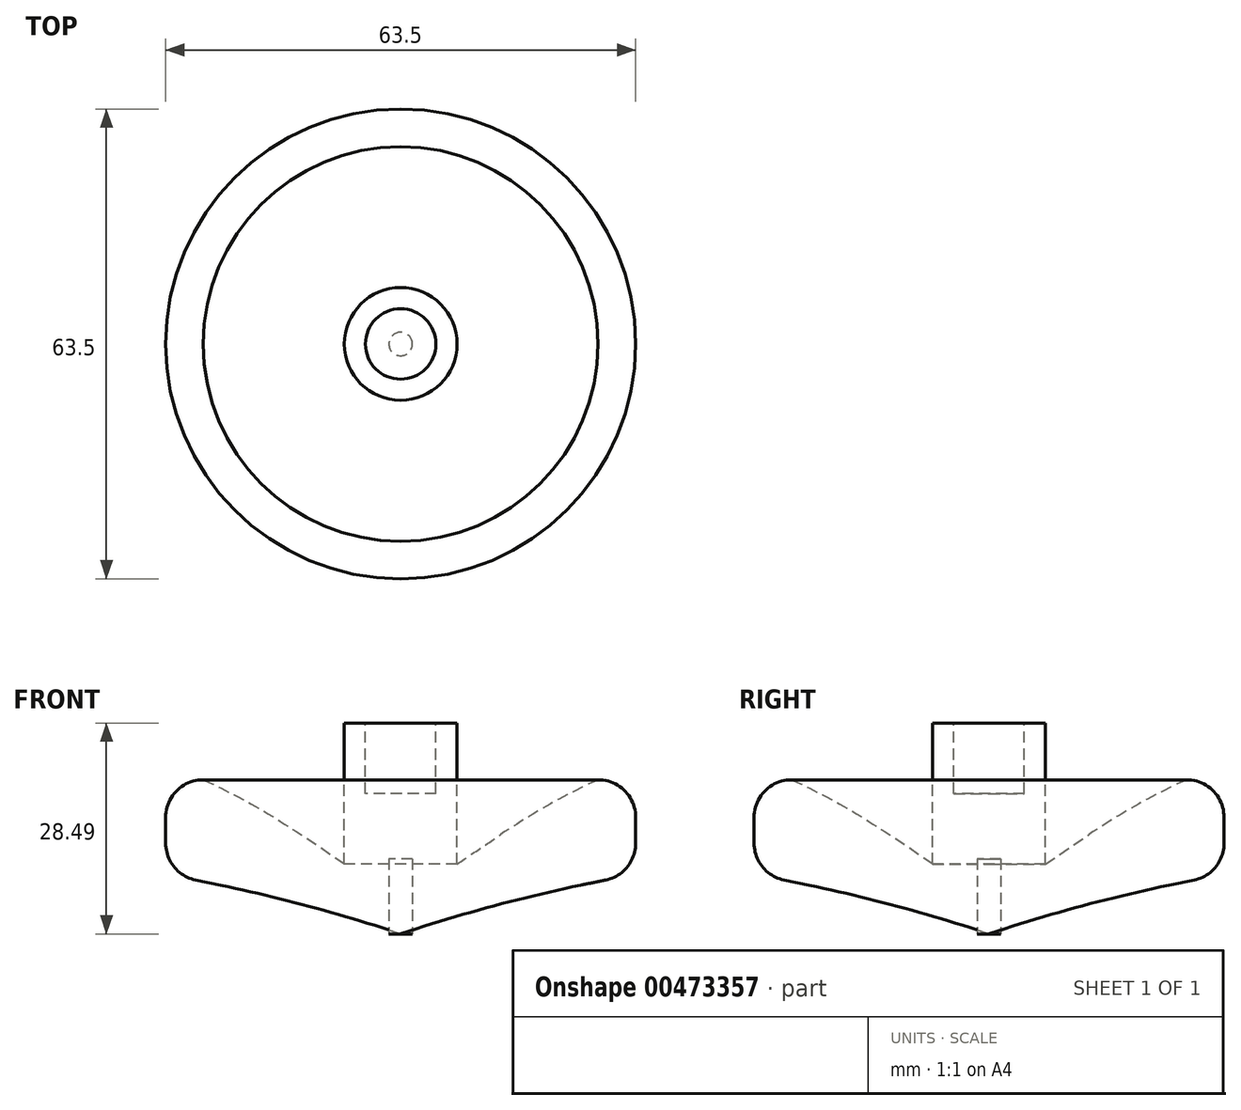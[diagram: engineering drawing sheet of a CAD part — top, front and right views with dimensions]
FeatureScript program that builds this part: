
annotation { "Feature Type Name" : "Feature", "Feature Type Description" : "" }
export const myFeature = defineFeature(function(context is Context, id is Id, definition is map)
    precondition{}
    {
        {
            var Q0;
            Q0=qCreatedBy(makeId("Front.planeOp"),FACE);
            var sketch = newSketch(context, id + "F0", { "sketchPlane" : qUnion([Q0])});
            skLineSegment(sketch, "E0", {"start": v(31.75, 8.13) * mm, "end": v(31.75, 20.83) * mm});
            skLineSegment(sketch, "E1", {"start": v(31.75, 20.83) * mm, "end": v(24.44, 20.83) * mm});
            skLineSegment(sketch, "E2", {"start": v(24.44, 20.83) * mm, "end": v(7.62, 9.44) * mm});
            skLineSegment(sketch, "E3", {"start": v(7.62, 9.44) * mm, "end": v(7.62, 28.49) * mm});
            skLineSegment(sketch, "E4", {"start": v(7.62, 28.49) * mm, "end": v(0, 28.49) * mm});
            skLineSegment(sketch, "E5", {"start": v(0, 28.49) * mm, "end": v(0, 0) * mm});
            skLineSegment(sketch, "E6", {"start": v(0, 0) * mm, "end": v(11.98, 4.02) * mm});
            skLineSegment(sketch, "E7", {"start": v(11.98, 4.02) * mm, "end": v(31.75, 8.13) * mm});
            skSolve(sketch);
        }
        {
            var Q0;
            Q0=qSketchRegion(id+"F0",true);
            var Q1;
            Q1=sQuery(id+"F0.wireOp",EDGE,"E5");
            revolve(context, id + "F1", {"entities" : qUnion([Q0]), "axis" : qUnion([Q1]), "revolveType" : RevolveType.FULL});
        }
        {
            var Q0;
            Q0=makeQuery(id+"F1.opRevolve","SWEPT_FACE",FACE,{"disambiguationData":[OSD([sQuery(id+"F0.wireOp",EDGE,"E0")])]});
            fillet(context, id + "F2", {"entities" : qUnion([Q0]), "radius" : 5.08 * mm, "tangentPropagation" : true, "allowEdgeOverflow" : false});
        }
        {
            var Q0;
            Q0=makeQuery(id+"F1.opRevolve","SWEPT_EDGE",EDGE,{"disambiguationData":[OSD([sQuery(id+"F0.wireOp",EDGE,"E1"),sQuery(id+"F0.wireOp",EDGE,"E2")])]});
            var Q1;
            {var subQ0=sQuery(id+"F0.wireOp",EDGE,"E1");Q1=makeQuery(id+"F2.opFillet","BLEND_EDGE",EDGE,{"blendedFrom":[makeQuery(id+"F1.opRevolve","SWEPT_EDGE",EDGE,{"disambiguationData":[OSD([sQuery(id+"F0.wireOp",EDGE,"E0"),subQ0])]}),makeQuery(id+"F1.opRevolve","SWEPT_FACE",FACE,{"disambiguationData":[OSD([subQ0])]})],"blendedInto":[makeQuery(id+"F1.opRevolve","SWEPT_FACE",FACE,{"disambiguationData":[OSD([subQ0])]})]});}
            fillet(context, id + "F3", {"entities" : qUnion([Q0, Q1]), "radius" : 91.44 * mm, "tangentPropagation" : true, "allowEdgeOverflow" : false});
        }
        {
            var Q0;
            Q0=makeQuery(id+"F1.opRevolve","SWEPT_EDGE",EDGE,{"disambiguationData":[OSD([sQuery(id+"F0.wireOp",EDGE,"E6"),sQuery(id+"F0.wireOp",EDGE,"E7")])]});
            var Q1;
            {var subQ0=sQuery(id+"F0.wireOp",EDGE,"E7");Q1=makeQuery(id+"F2.opFillet","BLEND_EDGE",EDGE,{"blendedFrom":[makeQuery(id+"F1.opRevolve","SWEPT_EDGE",EDGE,{"disambiguationData":[OSD([sQuery(id+"F0.wireOp",EDGE,"E0"),subQ0])]}),makeQuery(id+"F1.opRevolve","SWEPT_FACE",FACE,{"disambiguationData":[OSD([subQ0])]})],"blendedInto":[makeQuery(id+"F1.opRevolve","SWEPT_FACE",FACE,{"disambiguationData":[OSD([subQ0])]})]});}
            fillet(context, id + "F4", {"entities" : qUnion([Q0, Q1]), "radius" : 213.36 * mm, "tangentPropagation" : true, "allowEdgeOverflow" : false});
        }
        {
            var Q0;
            Q0=makeQuery(id+"F1.opRevolve","SWEPT_FACE",FACE,{"disambiguationData":[OSD([sQuery(id+"F0.wireOp",EDGE,"E4")])]});
            var sketch = newSketch(context, id + "F5", { "sketchPlane" : qUnion([Q0])});
            skCircle(sketch, "E8", {"center": v(0, 0) * mm, "radius": 4.76 * mm});
            skSolve(sketch);
        }
        {
            var Q0;
            Q0=qSketchRegion(id+"F5",true);
            extrude(context, id + "F6", {"entities" : qUnion([Q0]), "oppositeDirection" : true, "depth" : 9.52 * mm});
        }
        {
            var Q0;
            Q0=qCreatedBy(makeId("Top.planeOp"),FACE);
            var sketch = newSketch(context, id + "F7", { "sketchPlane" : qUnion([Q0])});
            skCircle(sketch, "E9", {"center": v(0, 0) * mm, "radius": 1.59 * mm});
            skSolve(sketch);
        }
        {
            var Q0;
            Q0=qSketchRegion(id+"F7",true);
            extrude(context, id + "F8", {"entities" : qUnion([Q0]), "depth" : 10.16 * mm});
        }
    });
